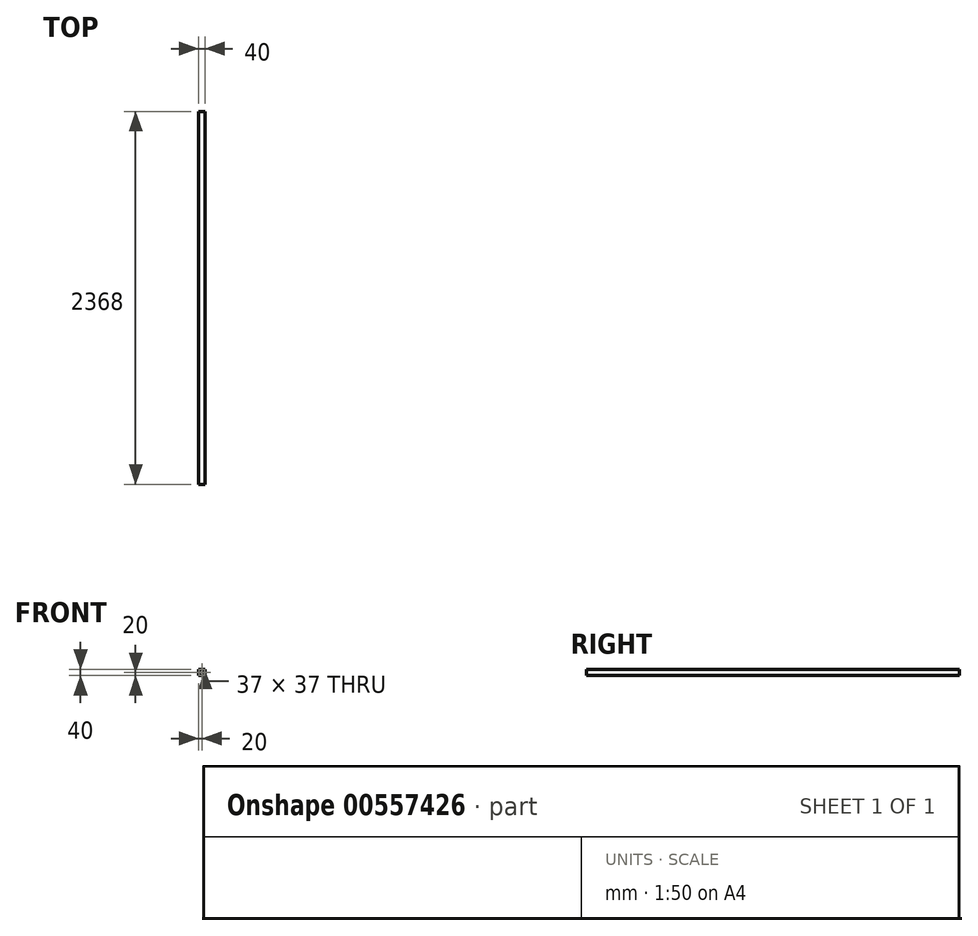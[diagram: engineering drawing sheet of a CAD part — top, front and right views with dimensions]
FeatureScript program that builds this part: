
annotation { "Feature Type Name" : "Feature", "Feature Type Description" : "" }
export const myFeature = defineFeature(function(context is Context, id is Id, definition is map)
    precondition{}
    {
        {
            var Q0;
            Q0=qCreatedBy(makeId("Front.planeOp"),FACE);
            var sketch = newSketch(context, id + "F0", { "sketchPlane" : qUnion([Q0])});
            skLineSegment(sketch, "E0.bottom", {"start": v(20, 20) * mm, "end": v(-20, 20) * mm});
            skLineSegment(sketch, "E0.top", {"start": v(20, -20) * mm, "end": v(-20, -20) * mm});
            skLineSegment(sketch, "E0.left", {"start": v(20, 20) * mm, "end": v(20, -20) * mm});
            skLineSegment(sketch, "E0.right", {"start": v(-20, 20) * mm, "end": v(-20, -20) * mm});
            skPoint(sketch, "E0.middle", {"position": v(0, 0) * mm});
            skLineSegment(sketch, "E1.0", {"start": v(-18.5, 18.5) * mm, "end": v(-18.5, -18.5) * mm});
            skLineSegment(sketch, "E1.1", {"start": v(18.5, 18.5) * mm, "end": v(-18.5, 18.5) * mm});
            skLineSegment(sketch, "E1.2", {"start": v(18.5, 18.5) * mm, "end": v(18.5, -18.5) * mm});
            skLineSegment(sketch, "E1.3", {"start": v(18.5, -18.5) * mm, "end": v(-18.5, -18.5) * mm});
            skSolve(sketch);
        }
        {
            var Q0;
            Q0=makeQuery(id+"F0.imprint","IMPRINT",FACE,{"disambiguationData":[TD([[makeQuery(id+"F0.imprint","IMPRINT",EDGE,{"derivedFrom":sQuery(id+"F0.wireOp",EDGE,"E0.bottom")}),1.0]])]});
            extrude(context, id + "F1", {"entities" : qUnion([Q0]), "endBound" : BoundingType.SYMMETRIC, "depth" : (2450 - 80 - 2) * mm, "offsetDistance" : 25 * mm});
        }
    });
